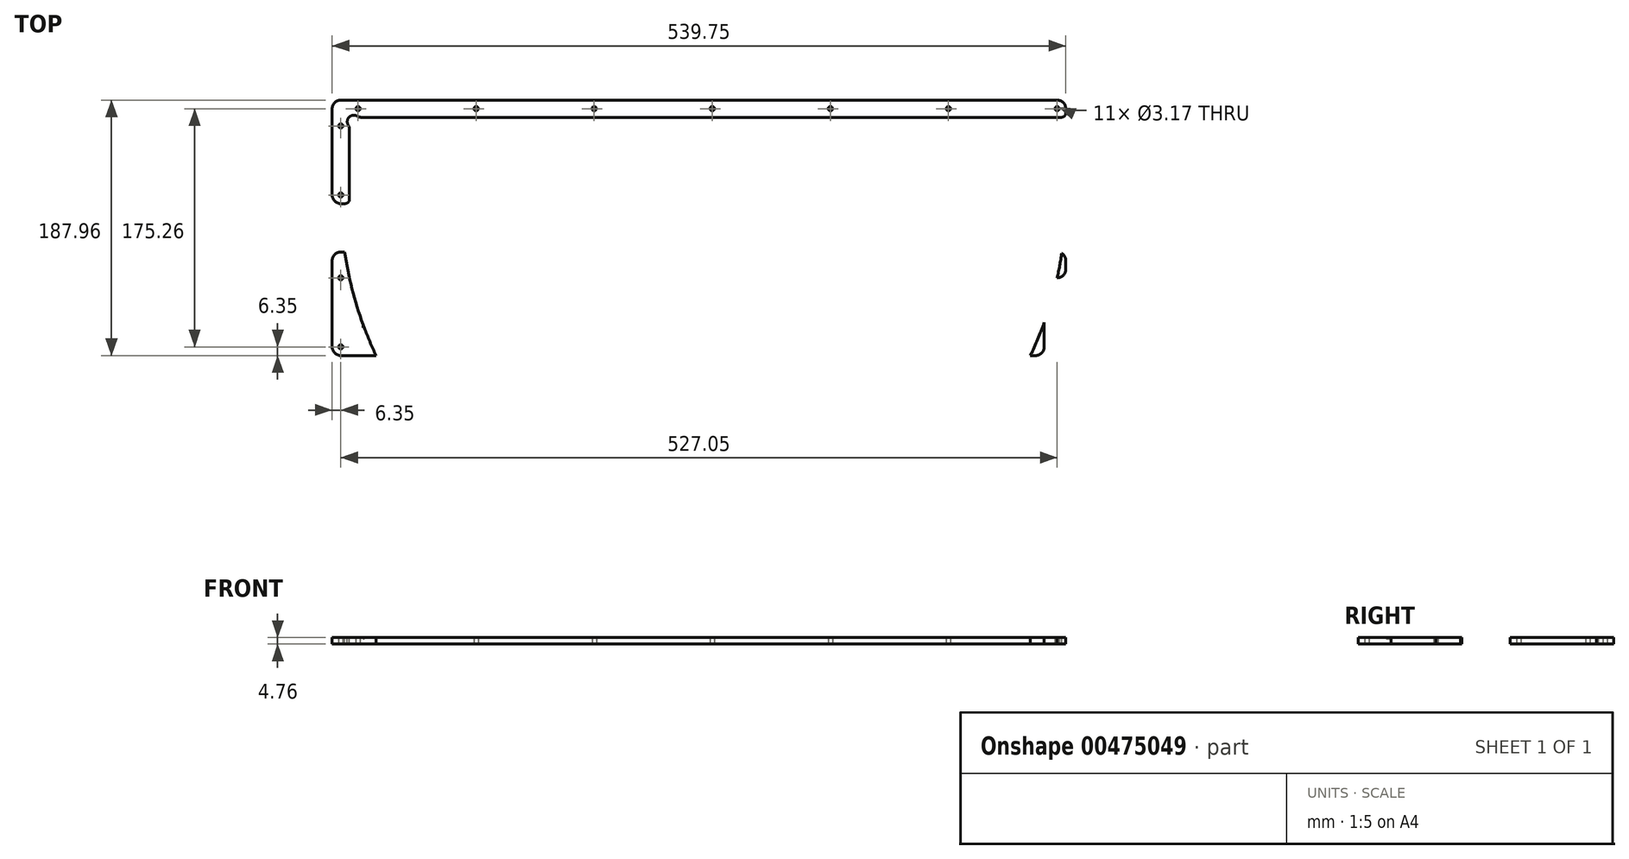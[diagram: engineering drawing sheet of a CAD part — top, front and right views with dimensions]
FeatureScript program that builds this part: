
annotation { "Feature Type Name" : "Feature", "Feature Type Description" : "" }
export const myFeature = defineFeature(function(context is Context, id is Id, definition is map)
    precondition{}
    {
        {
            var Q0;
            Q0=qCreatedBy(makeId("Top.planeOp"),FACE);
            var sketch = newSketch(context, id + "F0", { "sketchPlane" : qUnion([Q0])});
            skLineSegment(sketch, "E0.bottom", {"start": v(6.35, 0) * mm, "end": v(517.52, 0) * mm});
            skLineSegment(sketch, "E0.top", {"start": v(6.35, 76.2) * mm, "end": v(139.7, 76.2) * mm});
            skLineSegment(sketch, "E0.left", {"start": v(0, 6.35) * mm, "end": v(0, 69.85) * mm});
            skLineSegment(sketch, "E0.right", {"start": v(539.75, 63.5) * mm, "end": v(539.75, 69.85) * mm});
            skLineSegment(sketch, "E1.0", {"start": v(6.35, 69.85) * mm, "end": v(520.7, 69.85) * mm, "construction": true});
            skLineSegment(sketch, "E1.1", {"start": v(6.35, 0) * mm, "end": v(6.35, 69.85) * mm, "construction": true});
            skLineSegment(sketch, "E2.0", {"start": v(12.7, 63.5) * mm, "end": v(520.7, 63.5) * mm, "construction": true});
            skLineSegment(sketch, "E2.1", {"start": v(12.7, 0) * mm, "end": v(12.7, 63.5) * mm, "construction": true});
            skLineSegment(sketch, "E3.bottom", {"start": v(203.2, 14.29) * mm, "end": v(508, 14.29) * mm, "construction": true});
            skLineSegment(sketch, "E3.top", {"start": v(203.2, 33.34) * mm, "end": v(508, 33.34) * mm, "construction": true});
            skLineSegment(sketch, "E3.left", {"start": v(203.2, 14.29) * mm, "end": v(203.2, 33.34) * mm, "construction": true});
            skLineSegment(sketch, "E3.right", {"start": v(508, 14.29) * mm, "end": v(508, 33.34) * mm, "construction": true});
            skCircle(sketch, "E4", {"center": v(203.2, 33.34) * mm, "radius": 1.59 * mm});
            skCircle(sketch, "E5", {"center": v(203.2, 14.29) * mm, "radius": 1.59 * mm});
            skCircle(sketch, "E6", {"center": v(508, 14.29) * mm, "radius": 1.59 * mm});
            skCircle(sketch, "E7", {"center": v(508, 33.34) * mm, "radius": 1.59 * mm});
            skPoint(sketch, "E8.orphan", {"position": v(0, 76.2) * mm});
            skArc(sketch, "E9.filletArc", {"start": v(6.35, 76.2) * mm, "mid": v(1.86, 74.34) * mm, "end": v(0, 69.85) * mm});
            skPoint(sketch, "E10.visualSharp", {"position": v(0, 0) * mm});
            skArc(sketch, "E10.filletArc", {"start": v(0, 6.35) * mm, "mid": v(1.86, 1.86) * mm, "end": v(6.35, 0) * mm});
            skPoint(sketch, "E11.visualSharp", {"position": v(539.75, 0) * mm});
            skPoint(sketch, "E12.visualSharp", {"position": v(539.75, 76.2) * mm});
            skArc(sketch, "E12.filletArc", {"start": v(539.75, 69.85) * mm, "mid": v(537.9, 74.34) * mm, "end": v(533.4, 76.2) * mm});
            skLineSegment(sketch, "E13.bottom", {"start": v(152.4, 120.65) * mm, "end": v(228.6, 120.65) * mm});
            skLineSegment(sketch, "E13.left", {"start": v(146.05, 114.3) * mm, "end": v(146.05, 82.55) * mm});
            skLineSegment(sketch, "E13.right", {"start": v(234.95, 114.3) * mm, "end": v(234.95, 82.55) * mm});
            skLineSegment(sketch, "E14.trimOffspring", {"start": v(241.3, 76.2) * mm, "end": v(533.4, 76.2) * mm});
            skPoint(sketch, "E15.visualSharp", {"position": v(146.05, 76.2) * mm});
            skArc(sketch, "E15.filletArc", {"start": v(139.7, 76.2) * mm, "mid": v(144.2, 78.06) * mm, "end": v(146.05, 82.55) * mm});
            skPoint(sketch, "E16.visualSharp", {"position": v(146.05, 120.65) * mm});
            skArc(sketch, "E16.filletArc", {"start": v(152.4, 120.65) * mm, "mid": v(147.9, 118.8) * mm, "end": v(146.05, 114.3) * mm});
            skPoint(sketch, "E17.visualSharp", {"position": v(234.95, 120.65) * mm});
            skArc(sketch, "E17.filletArc", {"start": v(234.95, 114.3) * mm, "mid": v(233.1, 118.8) * mm, "end": v(228.6, 120.65) * mm});
            skPoint(sketch, "E18.visualSharp", {"position": v(234.95, 76.2) * mm});
            skArc(sketch, "E18.filletArc", {"start": v(234.95, 82.55) * mm, "mid": v(236.8, 78.06) * mm, "end": v(241.3, 76.2) * mm});
            skLineSegment(sketch, "E19", {"start": v(165.1, 106.36) * mm, "end": v(209.55, 106.36) * mm, "construction": true});
            skCircle(sketch, "E20", {"center": v(165.1, 106.36) * mm, "radius": 1.59 * mm});
            skCircle(sketch, "E21", {"center": v(209.55, 106.36) * mm, "radius": 1.59 * mm});
            skCircle(sketch, "E22", {"center": v(6.35, 6.35) * mm, "radius": 1.59 * mm});
            skCircle(sketch, "E23", {"center": v(6.35, 57.15) * mm, "radius": 1.59 * mm});
            skCircle(sketch, "E24.6.0.0", {"center": v(533.4, 69.85) * mm, "radius": 1.59 * mm});
            skLineSegment(sketch, "E24.direction1", {"start": v(6.35, 69.85) * mm, "end": v(93.66, 69.85) * mm, "construction": true});
            skLineSegment(sketch, "E25.bottom", {"start": v(463.55, 63.5) * mm, "end": v(247.65, 63.5) * mm});
            skLineSegment(sketch, "E25.top", {"start": v(463.55, 19.05) * mm, "end": v(247.65, 19.05) * mm});
            skLineSegment(sketch, "E25.left", {"start": v(469.9, 57.15) * mm, "end": v(469.9, 25.4) * mm});
            skLineSegment(sketch, "E25.right", {"start": v(241.3, 57.15) * mm, "end": v(241.3, 25.4) * mm});
            skPoint(sketch, "E26.visualSharp", {"position": v(241.3, 63.5) * mm});
            skArc(sketch, "E26.filletArc", {"start": v(247.65, 63.5) * mm, "mid": v(243.16, 61.64) * mm, "end": v(241.3, 57.15) * mm});
            skPoint(sketch, "E27.visualSharp", {"position": v(241.3, 19.05) * mm});
            skArc(sketch, "E27.filletArc", {"start": v(241.3, 25.4) * mm, "mid": v(243.16, 20.9) * mm, "end": v(247.65, 19.05) * mm});
            skPoint(sketch, "E28.visualSharp", {"position": v(469.9, 19.05) * mm});
            skArc(sketch, "E28.filletArc", {"start": v(463.55, 19.05) * mm, "mid": v(468.04, 20.9) * mm, "end": v(469.9, 25.4) * mm});
            skPoint(sketch, "E29.visualSharp", {"position": v(469.9, 63.5) * mm});
            skArc(sketch, "E29.filletArc", {"start": v(469.9, 57.15) * mm, "mid": v(468.04, 61.64) * mm, "end": v(463.55, 63.5) * mm});
            skLineSegment(sketch, "E30", {"start": v(533.4, 57.15) * mm, "end": v(530.23, 57.15) * mm});
            skLineSegment(sketch, "E31", {"start": v(523.88, 50.8) * mm, "end": v(523.88, 6.35) * mm});
            skPoint(sketch, "E32.visualSharp", {"position": v(539.75, 57.15) * mm});
            skArc(sketch, "E32.filletArc", {"start": v(533.4, 57.15) * mm, "mid": v(537.9, 59) * mm, "end": v(539.75, 63.5) * mm});
            skPoint(sketch, "E33.visualSharp", {"position": v(523.88, 57.15) * mm});
            skArc(sketch, "E33.filletArc", {"start": v(530.23, 57.15) * mm, "mid": v(525.73, 55.3) * mm, "end": v(523.88, 50.8) * mm});
            skPoint(sketch, "E34.visualSharp", {"position": v(523.88, 0) * mm});
            skArc(sketch, "E34.filletArc", {"start": v(517.53, 0) * mm, "mid": v(522.02, 1.86) * mm, "end": v(523.88, 6.35) * mm});
            skCircle(sketch, "E35", {"center": v(19.05, 69.85) * mm, "radius": 1.59 * mm});
            skCircle(sketch, "E36.1.0.0", {"center": v(105.92, 69.85) * mm, "radius": 1.59 * mm});
            skCircle(sketch, "E36.2.0.0", {"center": v(192.79, 69.85) * mm, "radius": 1.59 * mm});
            skCircle(sketch, "E36.3.0.0", {"center": v(279.65, 69.85) * mm, "radius": 1.59 * mm});
            skCircle(sketch, "E36.4.0.0", {"center": v(366.52, 69.85) * mm, "radius": 1.59 * mm});
            skCircle(sketch, "E36.5.0.0", {"center": v(453.4, 69.85) * mm, "radius": 1.59 * mm});
            skLineSegment(sketch, "E36.direction1", {"start": v(19.05, 69.85) * mm, "end": v(105.92, 69.85) * mm, "construction": true});
            skSolve(sketch);
        }
        {
            var Q0;
            Q0 = qSketchRegion(id + "F0", true);
            extrude(context, id + "F1", {"entities" : qUnion([Q0]), "depth" : 4.76 * mm});
        }
        {
            var Q0;
            Q0=makeQuery(id+"F1.opExtrude","CAP_FACE",FACE,{"disambiguationData":[OSD([sQuery(id+"F0.wireOp",EDGE,"E0.bottom"),sQuery(id+"F0.wireOp",EDGE,"E0.top"),sQuery(id+"F0.wireOp",EDGE,"E0.left"),sQuery(id+"F0.wireOp",EDGE,"E0.right"),sQuery(id+"F0.wireOp",EDGE,"E4"),sQuery(id+"F0.wireOp",EDGE,"E5"),sQuery(id+"F0.wireOp",EDGE,"E6"),sQuery(id+"F0.wireOp",EDGE,"E7"),sQuery(id+"F0.wireOp",EDGE,"n9yfQ6nm-pxFb-IRnj-wEPG-3ttQZnWaA1FG"),sQuery(id+"F0.wireOp",EDGE,"KsyP6wAw-adBe-FXAC-hm5t-zK6lRyagMJIB"),sQuery(id+"F0.wireOp",EDGE,"E9.filletArc"),sQuery(id+"F0.wireOp",EDGE,"65d9b9f6-b49e-443d-8538-84e0d76d2c0b.filletArc"),sQuery(id+"F0.wireOp",EDGE,"ddcd8abd-d16a-4f30-903d-530d8299df74.filletArc"),sQuery(id+"F0.wireOp",EDGE,"E10.filletArc"),sQuery(id+"F0.wireOp",EDGE,"E11.filletArc"),sQuery(id+"F0.wireOp",EDGE,"E12.filletArc"),sQuery(id+"F0.wireOp",EDGE,"E13.bottom"),sQuery(id+"F0.wireOp",EDGE,"E13.left"),sQuery(id+"F0.wireOp",EDGE,"E13.right"),sQuery(id+"F0.wireOp",EDGE,"E14.trimOffspring"),sQuery(id+"F0.wireOp",EDGE,"E15.filletArc"),sQuery(id+"F0.wireOp",EDGE,"E16.filletArc"),sQuery(id+"F0.wireOp",EDGE,"E17.filletArc"),sQuery(id+"F0.wireOp",EDGE,"E18.filletArc"),sQuery(id+"F0.wireOp",EDGE,"E20"),sQuery(id+"F0.wireOp",EDGE,"E21"),sQuery(id+"F0.wireOp",EDGE,"E22"),sQuery(id+"F0.wireOp",EDGE,"E23"),sQuery(id+"F0.wireOp",EDGE,"lADHZhyT-3w3l-RVtN-9cXv-kO8rpeL6DqHX"),sQuery(id+"F0.wireOp",EDGE,"E24.1.0.0"),sQuery(id+"F0.wireOp",EDGE,"E24.2.0.0"),sQuery(id+"F0.wireOp",EDGE,"E24.3.0.0"),sQuery(id+"F0.wireOp",EDGE,"E24.4.0.0"),sQuery(id+"F0.wireOp",EDGE,"E24.5.0.0"),sQuery(id+"F0.wireOp",EDGE,"E24.6.0.0")])],"isStart":false});
            var sketch = newSketch(context, id + "F2", { "sketchPlane" : qUnion([Q0])});
            skText(sketch, "E37", { "text": "DESIGN 316 - 100 DEG\nREGULAR ARM", "fontName": "AllertaStencil-Regular.ttf"});
            const initialGuessF2  = {"E37": [0.02119, 0.0432, 1, 0, 0.0127]};
            skSetInitialGuess(sketch, initialGuessF2);
            skSolve(sketch);
        }
        {
            var Q0;
            Q0 = qSketchRegion(id + "F2", true);
            extrude(context, id + "F3", {"entities" : qUnion([Q0]), "operationType" : NewBodyOperationType.REMOVE, "oppositeDirection" : true, "depth" : 0.8 * mm});
        }
        {
            var Q0;
            Q0=makeQuery(id+"F1.opExtrude","SWEPT_BODY",BODY,{"disambiguationData":[OSD([sQuery(id+"F0.wireOp",EDGE,"E0.bottom"),sQuery(id+"F0.wireOp",EDGE,"E0.top"),sQuery(id+"F0.wireOp",EDGE,"E0.left"),sQuery(id+"F0.wireOp",EDGE,"E0.right"),sQuery(id+"F0.wireOp",EDGE,"E4"),sQuery(id+"F0.wireOp",EDGE,"E5"),sQuery(id+"F0.wireOp",EDGE,"E6"),sQuery(id+"F0.wireOp",EDGE,"E7"),sQuery(id+"F0.wireOp",EDGE,"n9yfQ6nm-pxFb-IRnj-wEPG-3ttQZnWaA1FG"),sQuery(id+"F0.wireOp",EDGE,"KsyP6wAw-adBe-FXAC-hm5t-zK6lRyagMJIB"),sQuery(id+"F0.wireOp",EDGE,"E9.filletArc"),sQuery(id+"F0.wireOp",EDGE,"65d9b9f6-b49e-443d-8538-84e0d76d2c0b.filletArc"),sQuery(id+"F0.wireOp",EDGE,"ddcd8abd-d16a-4f30-903d-530d8299df74.filletArc"),sQuery(id+"F0.wireOp",EDGE,"E10.filletArc"),sQuery(id+"F0.wireOp",EDGE,"E11.filletArc"),sQuery(id+"F0.wireOp",EDGE,"E12.filletArc"),sQuery(id+"F0.wireOp",EDGE,"E13.bottom"),sQuery(id+"F0.wireOp",EDGE,"E13.left"),sQuery(id+"F0.wireOp",EDGE,"E13.right"),sQuery(id+"F0.wireOp",EDGE,"E14.trimOffspring"),sQuery(id+"F0.wireOp",EDGE,"E15.filletArc"),sQuery(id+"F0.wireOp",EDGE,"E16.filletArc"),sQuery(id+"F0.wireOp",EDGE,"E17.filletArc"),sQuery(id+"F0.wireOp",EDGE,"E18.filletArc"),sQuery(id+"F0.wireOp",EDGE,"E20"),sQuery(id+"F0.wireOp",EDGE,"E21"),sQuery(id+"F0.wireOp",EDGE,"E22"),sQuery(id+"F0.wireOp",EDGE,"E23"),sQuery(id+"F0.wireOp",EDGE,"lADHZhyT-3w3l-RVtN-9cXv-kO8rpeL6DqHX"),sQuery(id+"F0.wireOp",EDGE,"E24.1.0.0"),sQuery(id+"F0.wireOp",EDGE,"E24.2.0.0"),sQuery(id+"F0.wireOp",EDGE,"E24.3.0.0"),sQuery(id+"F0.wireOp",EDGE,"E24.4.0.0"),sQuery(id+"F0.wireOp",EDGE,"E24.5.0.0"),sQuery(id+"F0.wireOp",EDGE,"E24.6.0.0"),sQuery(id+"F0.wireOp",EDGE,"E25.bottom"),sQuery(id+"F0.wireOp",EDGE,"E25.top"),sQuery(id+"F0.wireOp",EDGE,"E25.left"),sQuery(id+"F0.wireOp",EDGE,"E25.right"),sQuery(id+"F0.wireOp",EDGE,"E26.filletArc"),sQuery(id+"F0.wireOp",EDGE,"E27.filletArc"),sQuery(id+"F0.wireOp",EDGE,"E28.filletArc"),sQuery(id+"F0.wireOp",EDGE,"E29.filletArc")])]});
            transform(context, id + "F4", {"entities" : qUnion([Q0]), "transformType" : TransformType.TRANSLATION_3D, "dx" : 0 * mm, "dy" : 111.76 * mm, "dz" : 0 * mm, "makeCopy" : true});
        }
        {
            var Q0;
            Q0=makeQuery(id+"F4.opPattern","COPY",FACE,{"derivedFrom":makeQuery(id+"F1.opExtrude","CAP_FACE",FACE,{"disambiguationData":[OSD([sQuery(id+"F0.wireOp",EDGE,"E0.bottom"),sQuery(id+"F0.wireOp",EDGE,"E0.top"),sQuery(id+"F0.wireOp",EDGE,"E0.left"),sQuery(id+"F0.wireOp",EDGE,"E0.right"),sQuery(id+"F0.wireOp",EDGE,"E4"),sQuery(id+"F0.wireOp",EDGE,"E5"),sQuery(id+"F0.wireOp",EDGE,"E6"),sQuery(id+"F0.wireOp",EDGE,"E7"),sQuery(id+"F0.wireOp",EDGE,"n9yfQ6nm-pxFb-IRnj-wEPG-3ttQZnWaA1FG"),sQuery(id+"F0.wireOp",EDGE,"KsyP6wAw-adBe-FXAC-hm5t-zK6lRyagMJIB"),sQuery(id+"F0.wireOp",EDGE,"E9.filletArc"),sQuery(id+"F0.wireOp",EDGE,"65d9b9f6-b49e-443d-8538-84e0d76d2c0b.filletArc"),sQuery(id+"F0.wireOp",EDGE,"ddcd8abd-d16a-4f30-903d-530d8299df74.filletArc"),sQuery(id+"F0.wireOp",EDGE,"E10.filletArc"),sQuery(id+"F0.wireOp",EDGE,"E11.filletArc"),sQuery(id+"F0.wireOp",EDGE,"E12.filletArc"),sQuery(id+"F0.wireOp",EDGE,"E13.bottom"),sQuery(id+"F0.wireOp",EDGE,"E13.left"),sQuery(id+"F0.wireOp",EDGE,"E13.right"),sQuery(id+"F0.wireOp",EDGE,"E14.trimOffspring"),sQuery(id+"F0.wireOp",EDGE,"E15.filletArc"),sQuery(id+"F0.wireOp",EDGE,"E16.filletArc"),sQuery(id+"F0.wireOp",EDGE,"E17.filletArc"),sQuery(id+"F0.wireOp",EDGE,"E18.filletArc"),sQuery(id+"F0.wireOp",EDGE,"E20"),sQuery(id+"F0.wireOp",EDGE,"E21"),sQuery(id+"F0.wireOp",EDGE,"E22"),sQuery(id+"F0.wireOp",EDGE,"E23"),sQuery(id+"F0.wireOp",EDGE,"lADHZhyT-3w3l-RVtN-9cXv-kO8rpeL6DqHX"),sQuery(id+"F0.wireOp",EDGE,"E24.1.0.0"),sQuery(id+"F0.wireOp",EDGE,"E24.2.0.0"),sQuery(id+"F0.wireOp",EDGE,"E24.3.0.0"),sQuery(id+"F0.wireOp",EDGE,"E24.4.0.0"),sQuery(id+"F0.wireOp",EDGE,"E24.5.0.0"),sQuery(id+"F0.wireOp",EDGE,"E24.6.0.0"),sQuery(id+"F0.wireOp",EDGE,"E25.bottom"),sQuery(id+"F0.wireOp",EDGE,"E25.top"),sQuery(id+"F0.wireOp",EDGE,"E25.left"),sQuery(id+"F0.wireOp",EDGE,"E25.right"),sQuery(id+"F0.wireOp",EDGE,"E26.filletArc"),sQuery(id+"F0.wireOp",EDGE,"E27.filletArc"),sQuery(id+"F0.wireOp",EDGE,"E28.filletArc"),sQuery(id+"F0.wireOp",EDGE,"E29.filletArc")])],"isStart":false}),"instanceName":"1"});
            var sketch = newSketch(context, id + "F5", { "sketchPlane" : qUnion([Q0])});
            skLineSegment(sketch, "E38.0", {"start": v(6.35, 111.76) * mm, "end": v(9.52, 111.76) * mm});
            skArc(sketch, "E38.1", {"start": v(6.35, 111.76) * mm, "mid": v(276.23, -151.76) * mm, "end": v(539.75, 118.11) * mm});
            skLineSegment(sketch, "E38.2", {"start": v(539.75, 118.11) * mm, "end": v(539.75, 178.44) * mm});
            skLineSegment(sketch, "E38.3", {"start": v(234.95, 226.06) * mm, "end": v(234.95, 194.31) * mm});
            skArc(sketch, "E38.4", {"start": v(234.95, 226.06) * mm, "mid": v(233.1, 230.55) * mm, "end": v(228.6, 232.41) * mm});
            skLineSegment(sketch, "E38.5", {"start": v(152.4, 232.41) * mm, "end": v(228.6, 232.41) * mm});
            skArc(sketch, "E38.6", {"start": v(152.4, 232.41) * mm, "mid": v(147.9, 230.55) * mm, "end": v(146.05, 226.06) * mm});
            skLineSegment(sketch, "E38.7", {"start": v(146.05, 226.06) * mm, "end": v(146.05, 194.31) * mm});
            skArc(sketch, "E38.8", {"start": v(139.7, 187.96) * mm, "mid": v(144.2, 189.82) * mm, "end": v(146.05, 194.31) * mm});
            skArc(sketch, "E38.9", {"start": v(234.95, 194.31) * mm, "mid": v(236.8, 189.82) * mm, "end": v(241.3, 187.96) * mm});
            skLineSegment(sketch, "E39", {"start": v(139.7, 187.96) * mm, "end": v(241.3, 187.96) * mm});
            skLineSegment(sketch, "E40", {"start": v(12.7, 114.94) * mm, "end": v(12.7, 166.36) * mm});
            skLineSegment(sketch, "E41", {"start": v(21.6, 175.26) * mm, "end": v(536.58, 175.26) * mm});
            skArc(sketch, "E42", {"start": v(18.33, 176.17) * mm, "mid": v(12.5, 175.45) * mm, "end": v(11.8, 169.63) * mm});
            skPoint(sketch, "E43.visualSharp", {"position": v(12.7, 168.54) * mm});
            skArc(sketch, "E43.filletArc", {"start": v(12.7, 166.36) * mm, "mid": v(12.47, 168.06) * mm, "end": v(11.8, 169.63) * mm});
            skPoint(sketch, "E44.visualSharp", {"position": v(19.42, 175.26) * mm});
            skArc(sketch, "E44.filletArc", {"start": v(18.33, 176.17) * mm, "mid": v(19.9, 175.5) * mm, "end": v(21.6, 175.26) * mm});
            skPoint(sketch, "E45.orphan", {"position": v(6.35, 111.76) * mm});
            skPoint(sketch, "E46.orphan", {"position": v(539.75, 181.61) * mm});
            skArc(sketch, "E47.filletArc", {"start": v(9.52, 111.76) * mm, "mid": v(11.77, 112.69) * mm, "end": v(12.7, 114.94) * mm});
            skArc(sketch, "E48.filletArc", {"start": v(536.58, 175.26) * mm, "mid": v(538.82, 176.19) * mm, "end": v(539.75, 178.44) * mm});
            skLineSegment(sketch, "E49", {"start": v(1.86, 186.1) * mm, "end": v(27.65, 160.3) * mm, "construction": true});
            skSolve(sketch);
        }
        {
            var Q0;
            Q0 = qSketchRegion(id + "F5", true);
            extrude(context, id + "F6", {"entities" : qUnion([Q0]), "operationType" : NewBodyOperationType.REMOVE, "endBound" : BoundingType.THROUGH_ALL, "oppositeDirection" : true, "depth" : 25.4 * mm});
        }
    });
